# Revit family: Enclosure-Screen-Teknion-Zones_ZNCHT-R2013
name_source: partatom
category: Furniture
revit_build: Autodesk Revit MEP 2013 (Build: 20130531_2115(x64)
units: mm (PartAtom-declared; Revit-internal decimal feet)

## types (2) — shared parameters
Assembly Code = E2020200
Height = 4' - 7"
Manufacturer = Teknion
Manufacturer Fax = 416.661.4586
Part Number = ZNCHT
Product Documentation Link = http://www.teknion.com
Product Line = Zones
Product Page URL = http://www.teknion.com
Series = Zones
Sustainability Data = http://www.teknion.com
URL = www.teknion.com
Warranty = http://www.teknion.com

## per-type parameters (varying)
| type | Depth | Description | Model |
| Full Configuration | 8' - 8" | Open Lounge Zone, 55 Height, Partial Slots, Full Configuration | ZNCHT55PF |
| Half Configuration | 2' - 8" | Open Lounge Zone, 55 Height, Partial Slots, Half Configuration | ZNCHT55PH |

type visibility flags (boolean, named after types; folded from table):
- Full Configuration: Yes: Full Configuration
- Half Configuration: Yes: (none)

## geometry (parser evidence)
native form markers: Blend x12, Sweep x6
no freeform markers — native parametric forms only
